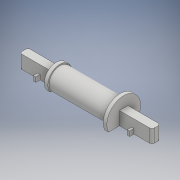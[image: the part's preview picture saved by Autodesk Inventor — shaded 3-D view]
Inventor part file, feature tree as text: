
AUTODESK INVENTOR PART (.ipt)
format: ipt  version: 2018 (Build 220112000, 112)  size: 181,760 bytes
history: native  units: mm
features: extrude x4, sketch x4, mirror x2, plane x1, thicken_offset x1, fillet x1, direct_edit x1, projected_geometry x1, move_body x1
ambient origin geometry x8: Origin, YZ Plane, XZ Plane, XY Plane, X Axis, Y Axis, Z Axis, Center Point
bodies: Solid1 (feature_tree)
feature tree (16):
  extrude  "Extrusion1"  Depth=7.0mm
  plane  "Work Plane1"
  extrude  "Extrusion2"  Depth=110.0mm TaperAngle=0.0deg
  extrude  "Extrusion3"  Depth=50.0mm TaperAngle=0.0deg
  mirror  "Mirror1"
  thicken_offset  "Thicken1"
  fillet  "Fillet1"  Radius=5.0mm
  direct_edit  "Direct Edit1"
  extrude  "Extrusion4"  Depth=4.0mm
  mirror  "Mirror2"
  sketch  "Sketch1"  dims[d0=20.0mm d1=7.0mm]
  sketch  "Sketch2"  dims[d2=10.0mm d3=110.0mm d4=0.0mm]
  sketch  "Sketch3"  dims[d5=18.0mm d6=50.0mm d7=0.0mm d8=5.0mm]
  sketch  "Sketch4"  dims[d9=3.0mm d10=0.0mm d11=4.0mm d12=4.0mm d14=0.0mm d15=0.0mm d16=1.0mm d17=2.0mm d18=80.0mm d19=14.0mm d20=2.0mm d21=4.0mm d22=0.0mm]
  projected_geometry  "Projected Loop1"
  move_body  "Move1"
